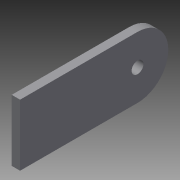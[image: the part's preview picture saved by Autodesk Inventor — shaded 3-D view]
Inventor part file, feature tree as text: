
AUTODESK INVENTOR PART (.ipt)
format: ipt  version: 2015 (Build 190159000, 159)  size: 84,992 bytes
history: native  units: mm
features: extrude x1, sketch x1
ambient origin geometry x8: Origin, YZ Plane, XZ Plane, XY Plane, X Axis, Y Axis, Z Axis, Center Point
bodies: Body1 (feature_tree)
feature tree (2):
  extrude  "Extrusion3"  Depth=6.0mm
  sketch  "Sketch3"  dims[d4=32.0mm d9=50.0mm d27=44.0mm d28=44.0mm d31=8.5mm d32=44.0mm d33=27.64mm d35=12.7mm d41=84.0mm d42=6.0mm d43=0.0mm]
